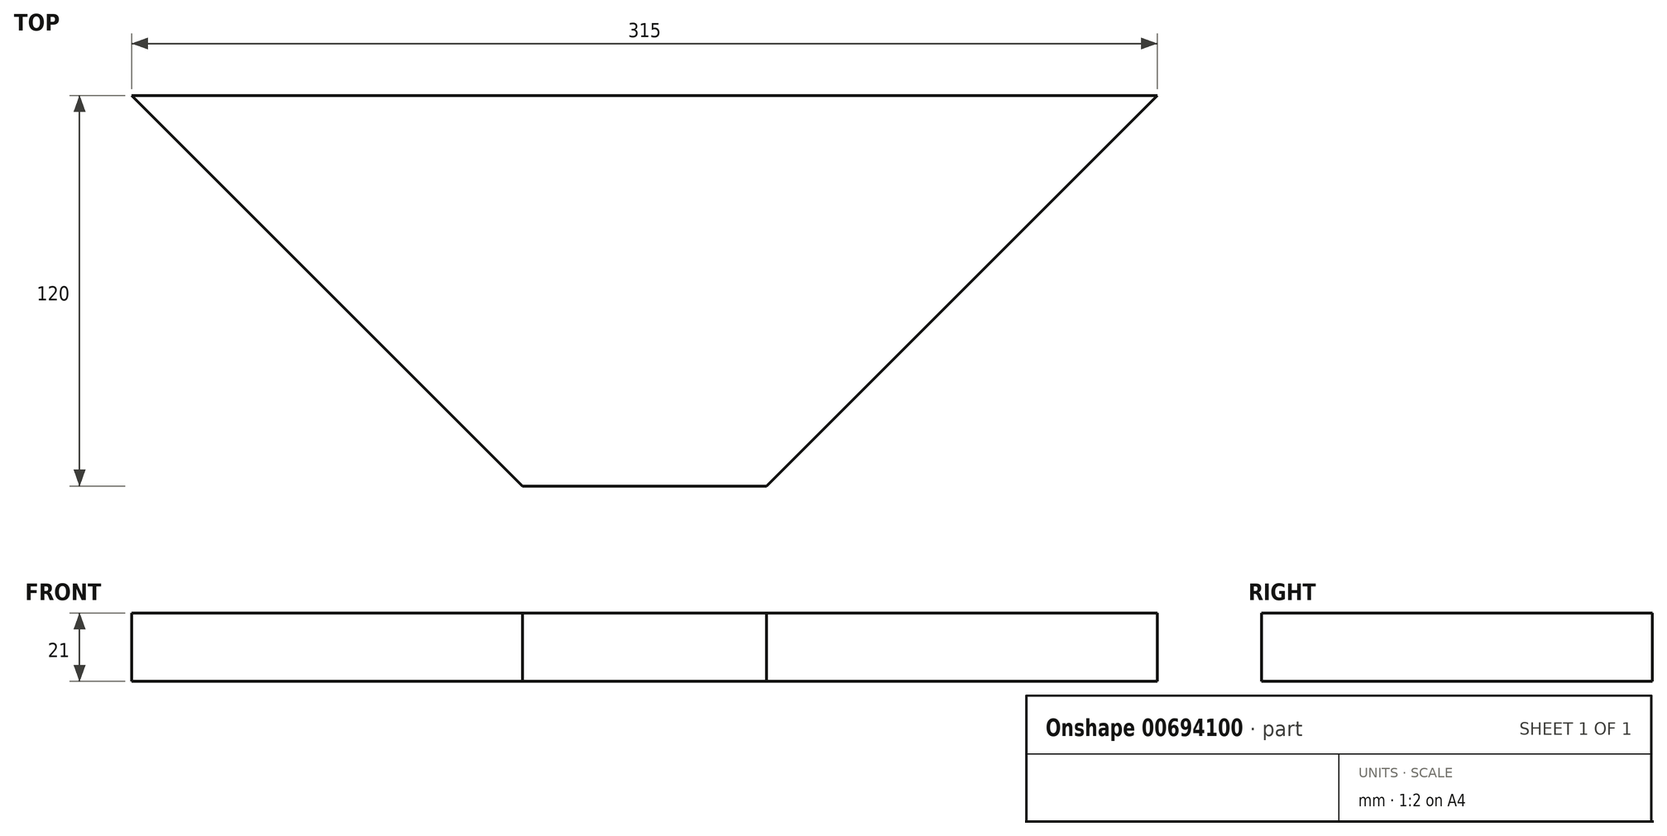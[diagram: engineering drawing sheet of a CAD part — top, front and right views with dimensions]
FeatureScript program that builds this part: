
annotation { "Feature Type Name" : "Feature", "Feature Type Description" : "" }
export const myFeature = defineFeature(function(context is Context, id is Id, definition is map)
    precondition{}
    {
        {
            var Q0;
            Q0=qCreatedBy(makeId("Top.planeOp"),FACE);
            var sketch = newSketch(context, id + "F0", { "sketchPlane" : qUnion([Q0])});
            skLineSegment(sketch, "E0", {"start": v(-37.5, -60) * mm, "end": v(37.5, -60) * mm});
            skLineSegment(sketch, "E1", {"start": v(37.5, -60) * mm, "end": v(157.5, 60) * mm});
            skLineSegment(sketch, "E2", {"start": v(157.5, 60) * mm, "end": v(-157.5, 60) * mm});
            skLineSegment(sketch, "E3", {"start": v(-157.5, 60) * mm, "end": v(-37.5, -60) * mm});
            skSolve(sketch);
        }
        {
            var Q0;
            Q0 = qSketchRegion(id + "F0", true);
            extrude(context, id + "F1", {"entities" : qUnion([Q0]), "depth" : 21 * mm, "offsetDistance" : 25 * mm});
        }
    });
